# Revit family: Grid_Drain-Sink-American_Standard-Heritage-7716020.002
name_source: partatom
category: Plumbing Fixtures
units: mm (PartAtom-declared; Revit-internal decimal feet)

## family parameters
Always vertical = No
Cut with Voids When Loaded = No
OmniClass Number = 23.70.50.21.24
OmniClass Title = Waste Water Drains
Part Type = Normal
Room Calculation Point = No
Round Connector Dimension = Use Diameter
Shared = Yes
Work Plane-Based = Yes

## types (1)
- 7716020.002
    Assembly Code = D2030400
    CW Connection = Yes
    CWFU = 2
    Cost = $0
    Default Elevation = 0"
    Description = Grid Drain With Overflow For Sinks
    Finish = Brass-American Standard-002-Polished Chrome
    HW Connection = Yes
    HWFU = 2
    Height = 6 13/16"
    IAPMO Compliance = ASME A112.18.2, CSA B 125.2
    Input Length = 4"
    Manufacturer = American Standard
    Material = Brass-American Standard-002-Polished Chrome
    Min Max Adjusted Length = 1 1/2"
    Model = 7716020.002
    Product Documentation Link = https://lixil.cdn.celum.cloud
    Product URL = https://www.americanstandard.ca
    Revised Date = 09/25/2024
    URL = https://www.americanstandard.ca
    Vent Connection = No
    WFU = 3
    Waste Connection = Yes
    Width = 1 1/2"

## geometry (parser evidence)
native form markers: Sweep x3
no freeform markers — native parametric forms only
